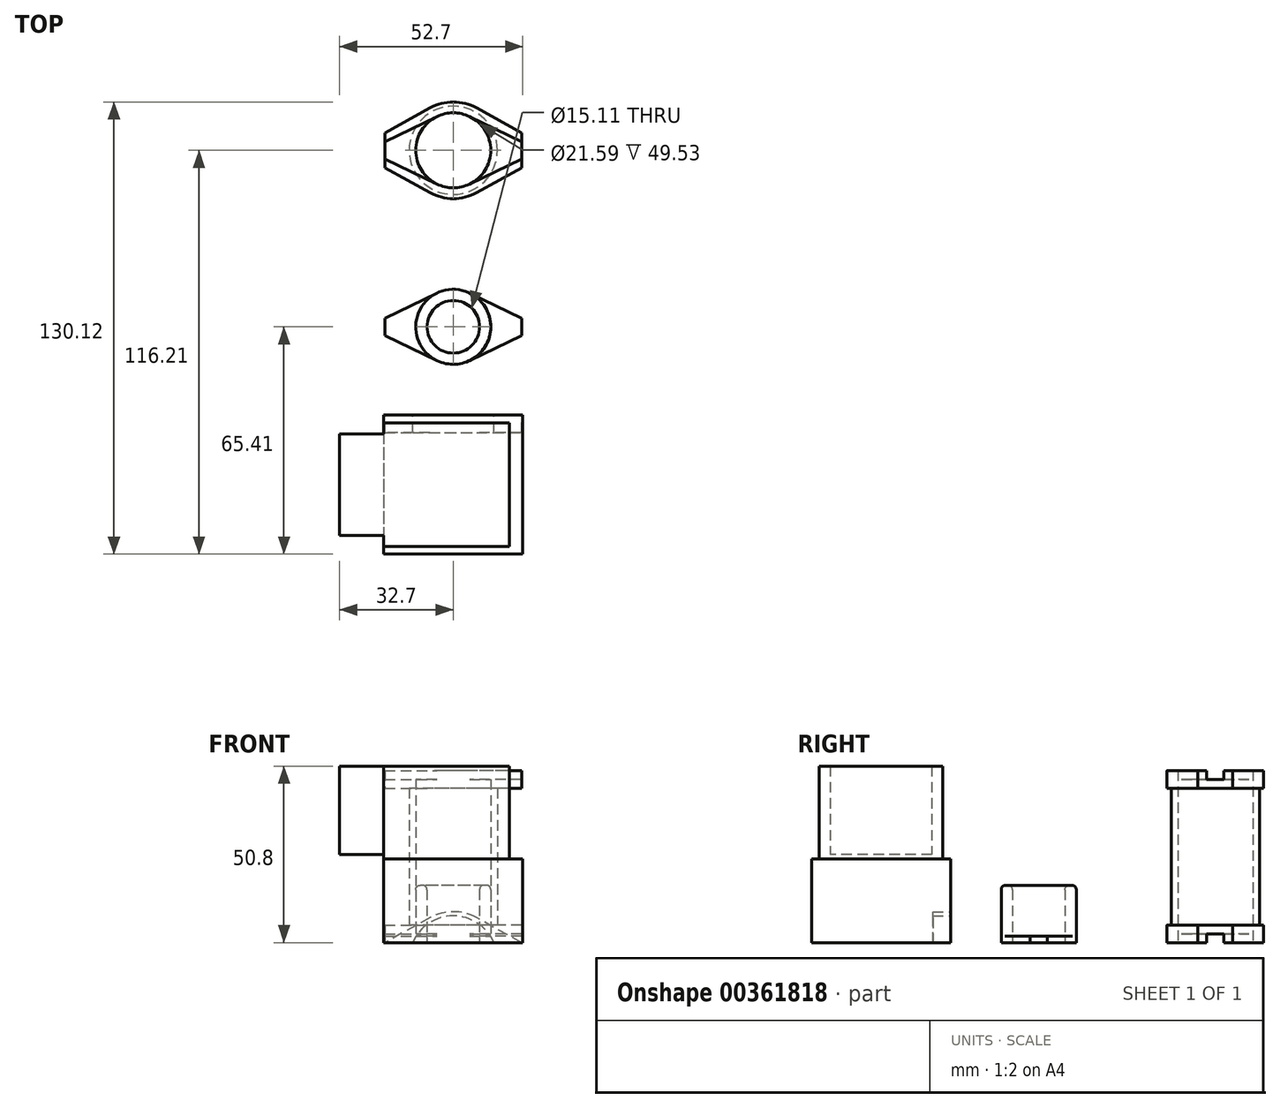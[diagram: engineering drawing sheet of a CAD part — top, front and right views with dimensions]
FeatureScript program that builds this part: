
annotation { "Feature Type Name" : "Feature", "Feature Type Description" : "" }
export const myFeature = defineFeature(function(context is Context, id is Id, definition is map)
    precondition{}
    {
        {
            var Q0;
            Q0=qCreatedBy(makeId("Top.planeOp"),FACE);
            var sketch = newSketch(context, id + "F0", { "sketchPlane" : qUnion([Q0])});
            skCircle(sketch, "E0", {"center": v(0, 0) * mm, "radius": 7.56 * mm});
            skCircle(sketch, "E1", {"center": v(0, 0) * mm, "radius": 10.8 * mm});
            skLineSegment(sketch, "E2", {"start": v(-19.69, 2.48) * mm, "end": v(-19.69, -2.48) * mm});
            skPoint(sketch, "E3", {"position": v(-19.69, 0) * mm});
            skLineSegment(sketch, "E4", {"start": v(-19.69, 2.48) * mm, "end": v(0, 11.99) * mm});
            skLineSegment(sketch, "E5", {"start": v(-19.69, -2.48) * mm, "end": v(0, -11.99) * mm});
            skPoint(sketch, "E6.MirrorP", {"position": v(19.69, 0) * mm});
            skLineSegment(sketch, "E7.MirrorCS", {"start": v(19.69, 2.48) * mm, "end": v(19.69, -2.48) * mm});
            skLineSegment(sketch, "E8.MirrorCS", {"start": v(19.69, 2.48) * mm, "end": v(0, 11.99) * mm});
            skLineSegment(sketch, "E9.MirrorCS", {"start": v(19.69, -2.48) * mm, "end": v(0, -11.99) * mm});
            skSolve(sketch);
        }
        {
            var Q0;
            {var subQ5=sQuery(id+"F0.wireOp",EDGE,"E2");Q0=makeQuery(id+"F0.imprint","IMPRINT",FACE,{"disambiguationData":[TD([[makeQuery(id+"F0.imprint","IMPRINT",EDGE,{"derivedFrom":subQ5}),1.0]])]});}
            var Q1;
            {var subQ5=sQuery(id+"F0.wireOp",EDGE,"E7.MirrorCS");Q1=makeQuery(id+"F0.imprint","IMPRINT",FACE,{"disambiguationData":[TD([[makeQuery(id+"F0.imprint","IMPRINT",EDGE,{"derivedFrom":subQ5}),-1.0]])]});}
            extrude(context, id + "F1", {"entities" : qUnion([Q0, Q1]), "depth" : 1.9 * mm, "offsetDistance" : 25.4 * mm});
        }
        {
            var Q0;
            Q0=makeQuery(id+"F0.imprint","IMPRINT",FACE,{"disambiguationData":[TD([[makeQuery(id+"F0.imprint","IMPRINT",EDGE,{"derivedFrom":sQuery(id+"F0.wireOp",EDGE,"E0")}),-1.0]])]});
            extrude(context, id + "F2", {"entities" : qUnion([Q0]), "operationType" : NewBodyOperationType.ADD, "depth" : 16.5 * mm, "offsetDistance" : 25.4 * mm});
        }
        {
            var Q0;
            Q0=makeQuery(id+"F2.opExtrude","CAP_EDGE",EDGE,{"disambiguationData":[OSD([sQuery(id+"F0.wireOp",EDGE,"E0")])],"isStart":false});
            var Q1;
            Q1=makeQuery(id+"F2.opExtrude","CAP_EDGE",EDGE,{"disambiguationData":[OSD([sQuery(id+"F0.wireOp",EDGE,"E1")])],"isStart":false});
            fillet(context, id + "F3", {"entities" : qUnion([Q0, Q1]), "radius" : 1.27 * mm, "tangentPropagation" : true, "allowEdgeOverflow" : false});
        }
        {
            var Q0;
            Q0=qCreatedBy(makeId("Top.planeOp"),FACE);
            var sketch = newSketch(context, id + "F4", { "sketchPlane" : qUnion([Q0])});
            skCircle(sketch, "E10", {"center": v(0, 50.8) * mm, "radius": 10.8 * mm});
            skLineSegment(sketch, "E11", {"start": v(-19.69, 53.28) * mm, "end": v(-19.69, 48.32) * mm});
            skPoint(sketch, "E12", {"position": v(-19.69, 50.8) * mm});
            skLineSegment(sketch, "E13", {"start": v(-19.69, 50.8) * mm, "end": v(0, 50.8) * mm, "construction": true});
            skLineSegment(sketch, "E14", {"start": v(0, 0) * mm, "end": v(-19.69, 0) * mm, "construction": true});
            skLineSegment(sketch, "E15", {"start": v(-19.69, 53.28) * mm, "end": v(0, 62.79) * mm});
            skLineSegment(sketch, "E16", {"start": v(-19.69, 48.32) * mm, "end": v(0, 38.81) * mm});
            skLineSegment(sketch, "E17.MirrorCS", {"start": v(19.69, 53.28) * mm, "end": v(19.69, 48.32) * mm});
            skPoint(sketch, "E18.MirrorP", {"position": v(19.69, 50.8) * mm});
            skLineSegment(sketch, "E19.MirrorCS", {"start": v(19.69, 53.28) * mm, "end": v(0, 62.79) * mm});
            skLineSegment(sketch, "E20.MirrorCS", {"start": v(19.69, 48.32) * mm, "end": v(0, 38.81) * mm});
            skLineSegment(sketch, "E21.MirrorCS", {"start": v(19.69, 50.8) * mm, "end": v(0, 50.8) * mm, "construction": true});
            skCircle(sketch, "E22", {"center": v(0, 50.8) * mm, "radius": 13.9 * mm});
            skLineSegment(sketch, "E23", {"start": v(-19.68, 55.82) * mm, "end": v(-19.68, 45.78) * mm});
            skPoint(sketch, "E24", {"position": v(-19.68, 50.8) * mm});
            skLineSegment(sketch, "E25", {"start": v(-19.68, 50.8) * mm, "end": v(0, 50.8) * mm, "construction": true});
            skLineSegment(sketch, "E26", {"start": v(-19.68, 55.82) * mm, "end": v(0, 66.69) * mm});
            skLineSegment(sketch, "E27", {"start": v(-19.69, 45.78) * mm, "end": v(0, 34.91) * mm});
            skLineSegment(sketch, "E28.MirrorCS", {"start": v(19.68, 55.82) * mm, "end": v(19.68, 45.78) * mm});
            skPoint(sketch, "E29.MirrorP", {"position": v(19.68, 50.8) * mm});
            skLineSegment(sketch, "E30.MirrorCS", {"start": v(19.68, 55.82) * mm, "end": v(0, 66.69) * mm});
            skLineSegment(sketch, "E31.MirrorCS", {"start": v(19.68, 45.78) * mm, "end": v(0, 34.91) * mm});
            skLineSegment(sketch, "E32.MirrorCS", {"start": v(19.68, 50.8) * mm, "end": v(0, 50.8) * mm, "construction": true});
            skCircle(sketch, "E33", {"center": v(0, 50.8) * mm, "radius": 12.7 * mm});
            skSolve(sketch);
        }
        {
            var Q0;
            {var subQ0=sQuery(id+"F4.wireOp",EDGE,"E23");var subQ1=sQuery(id+"F4.wireOp",EDGE,"E16");var subQ2=makeQuery(id+"F4.imprint","INTERSECT",VERTEX,{"derivedFrom":[subQ1,subQ0]});Q0=makeQuery(id+"F4.imprint","IMPRINT",FACE,{"disambiguationData":[TD([[makeQuery(id+"F4.imprint","IMPRINT",EDGE,{"disambiguationData":[TD([[subQ2,-1.0]])],"derivedFrom":subQ1}),-1.0]])]});}
            var Q1;
            {var subQ0=sQuery(id+"F4.wireOp",EDGE,"E28.MirrorCS");var subQ1=sQuery(id+"F4.wireOp",EDGE,"E20.MirrorCS");var subQ2=makeQuery(id+"F4.imprint","INTERSECT",VERTEX,{"derivedFrom":[subQ1,subQ0]});Q1=makeQuery(id+"F4.imprint","IMPRINT",FACE,{"disambiguationData":[TD([[makeQuery(id+"F4.imprint","IMPRINT",EDGE,{"disambiguationData":[TD([[subQ2,-1.0]])],"derivedFrom":subQ1}),1.0]])]});}
            var Q2;
            {var subQ0=sQuery(id+"F4.wireOp",EDGE,"E28.MirrorCS");var subQ1=sQuery(id+"F4.wireOp",EDGE,"E19.MirrorCS");var subQ2=makeQuery(id+"F4.imprint","INTERSECT",VERTEX,{"derivedFrom":[subQ1,subQ0]});Q2=makeQuery(id+"F4.imprint","IMPRINT",FACE,{"disambiguationData":[TD([[makeQuery(id+"F4.imprint","IMPRINT",EDGE,{"disambiguationData":[TD([[subQ2,-1.0]])],"derivedFrom":subQ1}),-1.0]])]});}
            var Q3;
            {var subQ0=sQuery(id+"F4.wireOp",EDGE,"E23");var subQ1=sQuery(id+"F4.wireOp",EDGE,"E15");var subQ2=makeQuery(id+"F4.imprint","INTERSECT",VERTEX,{"derivedFrom":[subQ1,subQ0]});Q3=makeQuery(id+"F4.imprint","IMPRINT",FACE,{"disambiguationData":[TD([[makeQuery(id+"F4.imprint","IMPRINT",EDGE,{"disambiguationData":[TD([[subQ2,-1.0]])],"derivedFrom":subQ1}),1.0]])]});}
            var Q4;
            {var subQ0=sQuery(id+"F4.wireOp",EDGE,"E23");var subQ1=sQuery(id+"F4.wireOp",EDGE,"E15");var subQ2=makeQuery(id+"F4.imprint","INTERSECT",VERTEX,{"derivedFrom":[subQ1,subQ0]});Q4=makeQuery(id+"F4.imprint","IMPRINT",FACE,{"disambiguationData":[TD([[makeQuery(id+"F4.imprint","IMPRINT",EDGE,{"disambiguationData":[TD([[subQ2,-1.0]])],"derivedFrom":subQ1}),-1.0]])]});}
            var Q5;
            {var subQ0=sQuery(id+"F4.wireOp",EDGE,"E28.MirrorCS");var subQ1=sQuery(id+"F4.wireOp",EDGE,"E19.MirrorCS");var subQ2=makeQuery(id+"F4.imprint","INTERSECT",VERTEX,{"derivedFrom":[subQ1,subQ0]});Q5=makeQuery(id+"F4.imprint","IMPRINT",FACE,{"disambiguationData":[TD([[makeQuery(id+"F4.imprint","IMPRINT",EDGE,{"disambiguationData":[TD([[subQ2,-1.0]])],"derivedFrom":subQ1}),1.0]])]});}
            var Q6;
            {var subQ0=sQuery(id+"F4.wireOp",EDGE,"E22");var subQ1=sQuery(id+"F4.wireOp",EDGE,"E15");var subQ2=makeQuery(id+"F4.imprint","INTERSECT",VERTEX,{"derivedFrom":[subQ1,subQ0]});Q6=makeQuery(id+"F4.imprint","IMPRINT",FACE,{"disambiguationData":[TD([[makeQuery(id+"F4.imprint","IMPRINT",EDGE,{"disambiguationData":[TD([[subQ2,-1.0]])],"derivedFrom":subQ1}),-1.0]])]});}
            var Q7;
            {var subQ0=sQuery(id+"F4.wireOp",EDGE,"E22");var subQ7=sQuery(id+"F4.wireOp",EDGE,"E15");var subQ9=makeQuery(id+"F4.imprint","INTERSECT",VERTEX,{"derivedFrom":[subQ7,subQ0]});Q7=makeQuery(id+"F4.imprint","IMPRINT",FACE,{"disambiguationData":[TD([[makeQuery(id+"F4.imprint","IMPRINT",EDGE,{"disambiguationData":[TD([[subQ9,-1.0]])],"derivedFrom":subQ7}),1.0]])]});}
            var Q8;
            {var subQ0=sQuery(id+"F4.wireOp",EDGE,"E15");var subQ1=sQuery(id+"F4.wireOp",EDGE,"E10");var subQ2=makeQuery(id+"F4.imprint","INTERSECT",VERTEX,{"derivedFrom":[subQ1,subQ0]});Q8=makeQuery(id+"F4.imprint","IMPRINT",FACE,{"disambiguationData":[TD([[makeQuery(id+"F4.imprint","IMPRINT",EDGE,{"disambiguationData":[TD([[subQ2,-1.0]])],"derivedFrom":subQ1}),-1.0]])]});}
            var Q9;
            {var subQ1=sQuery(id+"F4.wireOp",EDGE,"E15");var subQ3=sQuery(id+"F4.wireOp",EDGE,"E10");var subQ7=makeQuery(id+"F4.imprint","INTERSECT",VERTEX,{"derivedFrom":[subQ3,subQ1]});Q9=makeQuery(id+"F4.imprint","IMPRINT",FACE,{"disambiguationData":[TD([[makeQuery(id+"F4.imprint","IMPRINT",EDGE,{"disambiguationData":[TD([[subQ7,1.0]])],"derivedFrom":subQ1}),1.0]])]});}
            var Q10;
            {var subQ0=sQuery(id+"F4.wireOp",EDGE,"E15");var subQ1=sQuery(id+"F4.wireOp",EDGE,"E10");var subQ2=makeQuery(id+"F4.imprint","INTERSECT",VERTEX,{"derivedFrom":[subQ1,subQ0]});Q10=makeQuery(id+"F4.imprint","IMPRINT",FACE,{"disambiguationData":[TD([[makeQuery(id+"F4.imprint","IMPRINT",EDGE,{"disambiguationData":[TD([[subQ2,1.0]])],"derivedFrom":subQ1}),-1.0]])]});}
            var Q11;
            {var subQ0=sQuery(id+"F4.wireOp",EDGE,"E10");var subQ1=makeQuery(id+"F4.imprint","INTERSECT",VERTEX,{"derivedFrom":[subQ0,sQuery(id+"F4.wireOp",EDGE,"E15")]});Q11=makeQuery(id+"F4.imprint","IMPRINT",FACE,{"disambiguationData":[TD([[makeQuery(id+"F4.imprint","IMPRINT",EDGE,{"disambiguationData":[TD([[subQ1,1.0]])],"derivedFrom":subQ0}),1.0]])]});}
            var Q12;
            {var subQ0=sQuery(id+"F4.wireOp",EDGE,"E16");var subQ1=sQuery(id+"F4.wireOp",EDGE,"E10");var subQ2=makeQuery(id+"F4.imprint","INTERSECT",VERTEX,{"derivedFrom":[subQ1,subQ0]});Q12=makeQuery(id+"F4.imprint","IMPRINT",FACE,{"disambiguationData":[TD([[makeQuery(id+"F4.imprint","IMPRINT",EDGE,{"disambiguationData":[TD([[subQ2,-1.0]])],"derivedFrom":subQ1}),-1.0]])]});}
            var Q13;
            {var subQ1=sQuery(id+"F4.wireOp",EDGE,"E16");var subQ3=sQuery(id+"F4.wireOp",EDGE,"E10");var subQ7=makeQuery(id+"F4.imprint","INTERSECT",VERTEX,{"derivedFrom":[subQ3,subQ1]});Q13=makeQuery(id+"F4.imprint","IMPRINT",FACE,{"disambiguationData":[TD([[makeQuery(id+"F4.imprint","IMPRINT",EDGE,{"disambiguationData":[TD([[subQ7,1.0]])],"derivedFrom":subQ1}),-1.0]])]});}
            var Q14;
            {var subQ0=sQuery(id+"F4.wireOp",EDGE,"E22");var subQ7=sQuery(id+"F4.wireOp",EDGE,"E16");var subQ8=makeQuery(id+"F4.imprint","INTERSECT",VERTEX,{"derivedFrom":[subQ7,subQ0]});Q14=makeQuery(id+"F4.imprint","IMPRINT",FACE,{"disambiguationData":[TD([[makeQuery(id+"F4.imprint","IMPRINT",EDGE,{"disambiguationData":[TD([[subQ8,-1.0]])],"derivedFrom":subQ7}),-1.0]])]});}
            var Q15;
            {var subQ0=sQuery(id+"F4.wireOp",EDGE,"E19.MirrorCS");var subQ1=sQuery(id+"F4.wireOp",EDGE,"E10");var subQ2=makeQuery(id+"F4.imprint","INTERSECT",VERTEX,{"derivedFrom":[subQ1,subQ0]});Q15=makeQuery(id+"F4.imprint","IMPRINT",FACE,{"disambiguationData":[TD([[makeQuery(id+"F4.imprint","IMPRINT",EDGE,{"disambiguationData":[TD([[subQ2,1.0]])],"derivedFrom":subQ1}),-1.0]])]});}
            var Q16;
            {var subQ0=sQuery(id+"F4.wireOp",EDGE,"E22");var subQ1=sQuery(id+"F4.wireOp",EDGE,"E19.MirrorCS");var subQ2=makeQuery(id+"F4.imprint","INTERSECT",VERTEX,{"derivedFrom":[subQ1,subQ0]});Q16=makeQuery(id+"F4.imprint","IMPRINT",FACE,{"disambiguationData":[TD([[makeQuery(id+"F4.imprint","IMPRINT",EDGE,{"disambiguationData":[TD([[subQ2,-1.0]])],"derivedFrom":subQ1}),1.0]])]});}
            extrude(context, id + "F5", {"entities" : qUnion([Q0, Q1, Q2, Q3, Q4, Q5, Q6, Q7, Q8, Q9, Q10, Q11, Q12, Q13, Q14, Q15, Q16]), "depth" : 49.53 * mm, "offsetDistance" : 25.4 * mm});
        }
        {
            var Q0;
            {var subQ0=sQuery(id+"F4.wireOp",EDGE,"E23");var subQ1=sQuery(id+"F4.wireOp",EDGE,"E16");var subQ2=makeQuery(id+"F4.imprint","INTERSECT",VERTEX,{"derivedFrom":[subQ1,subQ0]});Q0=makeQuery(id+"F4.imprint","IMPRINT",FACE,{"disambiguationData":[TD([[makeQuery(id+"F4.imprint","IMPRINT",EDGE,{"disambiguationData":[TD([[subQ2,-1.0]])],"derivedFrom":subQ1}),-1.0]])]});}
            var Q1;
            {var subQ0=sQuery(id+"F4.wireOp",EDGE,"E23");var subQ1=sQuery(id+"F4.wireOp",EDGE,"E15");var subQ2=makeQuery(id+"F4.imprint","INTERSECT",VERTEX,{"derivedFrom":[subQ1,subQ0]});Q1=makeQuery(id+"F4.imprint","IMPRINT",FACE,{"disambiguationData":[TD([[makeQuery(id+"F4.imprint","IMPRINT",EDGE,{"disambiguationData":[TD([[subQ2,-1.0]])],"derivedFrom":subQ1}),-1.0]])]});}
            var Q2;
            {var subQ0=sQuery(id+"F4.wireOp",EDGE,"E23");var subQ1=sQuery(id+"F4.wireOp",EDGE,"E15");var subQ2=makeQuery(id+"F4.imprint","INTERSECT",VERTEX,{"derivedFrom":[subQ1,subQ0]});Q2=makeQuery(id+"F4.imprint","IMPRINT",FACE,{"disambiguationData":[TD([[makeQuery(id+"F4.imprint","IMPRINT",EDGE,{"disambiguationData":[TD([[subQ2,-1.0]])],"derivedFrom":subQ1}),1.0]])]});}
            var Q3;
            {var subQ0=sQuery(id+"F4.wireOp",EDGE,"E28.MirrorCS");var subQ1=sQuery(id+"F4.wireOp",EDGE,"E19.MirrorCS");var subQ2=makeQuery(id+"F4.imprint","INTERSECT",VERTEX,{"derivedFrom":[subQ1,subQ0]});Q3=makeQuery(id+"F4.imprint","IMPRINT",FACE,{"disambiguationData":[TD([[makeQuery(id+"F4.imprint","IMPRINT",EDGE,{"disambiguationData":[TD([[subQ2,-1.0]])],"derivedFrom":subQ1}),-1.0]])]});}
            var Q4;
            {var subQ0=sQuery(id+"F4.wireOp",EDGE,"E28.MirrorCS");var subQ1=sQuery(id+"F4.wireOp",EDGE,"E19.MirrorCS");var subQ2=makeQuery(id+"F4.imprint","INTERSECT",VERTEX,{"derivedFrom":[subQ1,subQ0]});Q4=makeQuery(id+"F4.imprint","IMPRINT",FACE,{"disambiguationData":[TD([[makeQuery(id+"F4.imprint","IMPRINT",EDGE,{"disambiguationData":[TD([[subQ2,-1.0]])],"derivedFrom":subQ1}),1.0]])]});}
            var Q5;
            {var subQ0=sQuery(id+"F4.wireOp",EDGE,"E28.MirrorCS");var subQ1=sQuery(id+"F4.wireOp",EDGE,"E20.MirrorCS");var subQ2=makeQuery(id+"F4.imprint","INTERSECT",VERTEX,{"derivedFrom":[subQ1,subQ0]});Q5=makeQuery(id+"F4.imprint","IMPRINT",FACE,{"disambiguationData":[TD([[makeQuery(id+"F4.imprint","IMPRINT",EDGE,{"disambiguationData":[TD([[subQ2,-1.0]])],"derivedFrom":subQ1}),1.0]])]});}
            var Q6;
            {var subQ0=sQuery(id+"F4.wireOp",EDGE,"E22");var subQ7=sQuery(id+"F4.wireOp",EDGE,"E16");var subQ8=makeQuery(id+"F4.imprint","INTERSECT",VERTEX,{"derivedFrom":[subQ7,subQ0]});Q6=makeQuery(id+"F4.imprint","IMPRINT",FACE,{"disambiguationData":[TD([[makeQuery(id+"F4.imprint","IMPRINT",EDGE,{"disambiguationData":[TD([[subQ8,-1.0]])],"derivedFrom":subQ7}),-1.0]])]});}
            var Q7;
            {var subQ0=sQuery(id+"F4.wireOp",EDGE,"E22");var subQ7=sQuery(id+"F4.wireOp",EDGE,"E15");var subQ9=makeQuery(id+"F4.imprint","INTERSECT",VERTEX,{"derivedFrom":[subQ7,subQ0]});Q7=makeQuery(id+"F4.imprint","IMPRINT",FACE,{"disambiguationData":[TD([[makeQuery(id+"F4.imprint","IMPRINT",EDGE,{"disambiguationData":[TD([[subQ9,-1.0]])],"derivedFrom":subQ7}),1.0]])]});}
            var Q8;
            {var subQ0=sQuery(id+"F4.wireOp",EDGE,"E22");var subQ1=sQuery(id+"F4.wireOp",EDGE,"E19.MirrorCS");var subQ2=makeQuery(id+"F4.imprint","INTERSECT",VERTEX,{"derivedFrom":[subQ1,subQ0]});Q8=makeQuery(id+"F4.imprint","IMPRINT",FACE,{"disambiguationData":[TD([[makeQuery(id+"F4.imprint","IMPRINT",EDGE,{"disambiguationData":[TD([[subQ2,-1.0]])],"derivedFrom":subQ1}),1.0]])]});}
            var Q9;
            {var subQ0=sQuery(id+"F4.wireOp",EDGE,"E22");var subQ1=sQuery(id+"F4.wireOp",EDGE,"E15");var subQ2=makeQuery(id+"F4.imprint","INTERSECT",VERTEX,{"derivedFrom":[subQ1,subQ0]});Q9=makeQuery(id+"F4.imprint","IMPRINT",FACE,{"disambiguationData":[TD([[makeQuery(id+"F4.imprint","IMPRINT",EDGE,{"disambiguationData":[TD([[subQ2,-1.0]])],"derivedFrom":subQ1}),-1.0]])]});}
            extrude(context, id + "F6", {"entities" : qUnion([Q0, Q1, Q2, Q3, Q4, Q5, Q6, Q7, Q8, Q9]), "operationType" : NewBodyOperationType.REMOVE, "depth" : 44.45 * mm, "offsetDistance" : 25.4 * mm});
        }
        {
            var Q0;
            {var subQ0=sQuery(id+"F4.wireOp",EDGE,"E23");var subQ1=sQuery(id+"F4.wireOp",EDGE,"E16");var subQ2=makeQuery(id+"F4.imprint","INTERSECT",VERTEX,{"derivedFrom":[subQ1,subQ0]});Q0=makeQuery(id+"F4.imprint","IMPRINT",FACE,{"disambiguationData":[TD([[makeQuery(id+"F4.imprint","IMPRINT",EDGE,{"disambiguationData":[TD([[subQ2,-1.0]])],"derivedFrom":subQ1}),-1.0]])]});}
            var Q1;
            {var subQ0=sQuery(id+"F4.wireOp",EDGE,"E22");var subQ7=sQuery(id+"F4.wireOp",EDGE,"E16");var subQ8=makeQuery(id+"F4.imprint","INTERSECT",VERTEX,{"derivedFrom":[subQ7,subQ0]});Q1=makeQuery(id+"F4.imprint","IMPRINT",FACE,{"disambiguationData":[TD([[makeQuery(id+"F4.imprint","IMPRINT",EDGE,{"disambiguationData":[TD([[subQ8,-1.0]])],"derivedFrom":subQ7}),-1.0]])]});}
            var Q2;
            {var subQ1=sQuery(id+"F4.wireOp",EDGE,"E16");var subQ3=sQuery(id+"F4.wireOp",EDGE,"E10");var subQ7=makeQuery(id+"F4.imprint","INTERSECT",VERTEX,{"derivedFrom":[subQ3,subQ1]});Q2=makeQuery(id+"F4.imprint","IMPRINT",FACE,{"disambiguationData":[TD([[makeQuery(id+"F4.imprint","IMPRINT",EDGE,{"disambiguationData":[TD([[subQ7,1.0]])],"derivedFrom":subQ1}),-1.0]])]});}
            var Q3;
            {var subQ0=sQuery(id+"F4.wireOp",EDGE,"E15");var subQ1=sQuery(id+"F4.wireOp",EDGE,"E10");var subQ2=makeQuery(id+"F4.imprint","INTERSECT",VERTEX,{"derivedFrom":[subQ1,subQ0]});Q3=makeQuery(id+"F4.imprint","IMPRINT",FACE,{"disambiguationData":[TD([[makeQuery(id+"F4.imprint","IMPRINT",EDGE,{"disambiguationData":[TD([[subQ2,-1.0]])],"derivedFrom":subQ1}),-1.0]])]});}
            var Q4;
            {var subQ0=sQuery(id+"F4.wireOp",EDGE,"E22");var subQ1=sQuery(id+"F4.wireOp",EDGE,"E15");var subQ2=makeQuery(id+"F4.imprint","INTERSECT",VERTEX,{"derivedFrom":[subQ1,subQ0]});Q4=makeQuery(id+"F4.imprint","IMPRINT",FACE,{"disambiguationData":[TD([[makeQuery(id+"F4.imprint","IMPRINT",EDGE,{"disambiguationData":[TD([[subQ2,-1.0]])],"derivedFrom":subQ1}),-1.0]])]});}
            var Q5;
            {var subQ0=sQuery(id+"F4.wireOp",EDGE,"E23");var subQ1=sQuery(id+"F4.wireOp",EDGE,"E15");var subQ2=makeQuery(id+"F4.imprint","INTERSECT",VERTEX,{"derivedFrom":[subQ1,subQ0]});Q5=makeQuery(id+"F4.imprint","IMPRINT",FACE,{"disambiguationData":[TD([[makeQuery(id+"F4.imprint","IMPRINT",EDGE,{"disambiguationData":[TD([[subQ2,-1.0]])],"derivedFrom":subQ1}),-1.0]])]});}
            var Q6;
            {var subQ0=sQuery(id+"F4.wireOp",EDGE,"E23");var subQ1=sQuery(id+"F4.wireOp",EDGE,"E15");var subQ2=makeQuery(id+"F4.imprint","INTERSECT",VERTEX,{"derivedFrom":[subQ1,subQ0]});Q6=makeQuery(id+"F4.imprint","IMPRINT",FACE,{"disambiguationData":[TD([[makeQuery(id+"F4.imprint","IMPRINT",EDGE,{"disambiguationData":[TD([[subQ2,-1.0]])],"derivedFrom":subQ1}),1.0]])]});}
            var Q7;
            {var subQ1=sQuery(id+"F4.wireOp",EDGE,"E15");var subQ3=sQuery(id+"F4.wireOp",EDGE,"E10");var subQ7=makeQuery(id+"F4.imprint","INTERSECT",VERTEX,{"derivedFrom":[subQ3,subQ1]});Q7=makeQuery(id+"F4.imprint","IMPRINT",FACE,{"disambiguationData":[TD([[makeQuery(id+"F4.imprint","IMPRINT",EDGE,{"disambiguationData":[TD([[subQ7,1.0]])],"derivedFrom":subQ1}),1.0]])]});}
            var Q8;
            {var subQ0=sQuery(id+"F4.wireOp",EDGE,"E22");var subQ7=sQuery(id+"F4.wireOp",EDGE,"E15");var subQ9=makeQuery(id+"F4.imprint","INTERSECT",VERTEX,{"derivedFrom":[subQ7,subQ0]});Q8=makeQuery(id+"F4.imprint","IMPRINT",FACE,{"disambiguationData":[TD([[makeQuery(id+"F4.imprint","IMPRINT",EDGE,{"disambiguationData":[TD([[subQ9,-1.0]])],"derivedFrom":subQ7}),1.0]])]});}
            var Q9;
            {var subQ0=sQuery(id+"F4.wireOp",EDGE,"E15");var subQ1=sQuery(id+"F4.wireOp",EDGE,"E10");var subQ2=makeQuery(id+"F4.imprint","INTERSECT",VERTEX,{"derivedFrom":[subQ1,subQ0]});Q9=makeQuery(id+"F4.imprint","IMPRINT",FACE,{"disambiguationData":[TD([[makeQuery(id+"F4.imprint","IMPRINT",EDGE,{"disambiguationData":[TD([[subQ2,1.0]])],"derivedFrom":subQ1}),-1.0]])]});}
            var Q10;
            {var subQ0=sQuery(id+"F4.wireOp",EDGE,"E10");var subQ1=makeQuery(id+"F4.imprint","INTERSECT",VERTEX,{"derivedFrom":[subQ0,sQuery(id+"F4.wireOp",EDGE,"E15")]});Q10=makeQuery(id+"F4.imprint","IMPRINT",FACE,{"disambiguationData":[TD([[makeQuery(id+"F4.imprint","IMPRINT",EDGE,{"disambiguationData":[TD([[subQ1,1.0]])],"derivedFrom":subQ0}),1.0]])]});}
            var Q11;
            {var subQ0=sQuery(id+"F4.wireOp",EDGE,"E19.MirrorCS");var subQ1=sQuery(id+"F4.wireOp",EDGE,"E10");var subQ2=makeQuery(id+"F4.imprint","INTERSECT",VERTEX,{"derivedFrom":[subQ1,subQ0]});Q11=makeQuery(id+"F4.imprint","IMPRINT",FACE,{"disambiguationData":[TD([[makeQuery(id+"F4.imprint","IMPRINT",EDGE,{"disambiguationData":[TD([[subQ2,1.0]])],"derivedFrom":subQ1}),-1.0]])]});}
            var Q12;
            {var subQ0=sQuery(id+"F4.wireOp",EDGE,"E22");var subQ1=sQuery(id+"F4.wireOp",EDGE,"E19.MirrorCS");var subQ2=makeQuery(id+"F4.imprint","INTERSECT",VERTEX,{"derivedFrom":[subQ1,subQ0]});Q12=makeQuery(id+"F4.imprint","IMPRINT",FACE,{"disambiguationData":[TD([[makeQuery(id+"F4.imprint","IMPRINT",EDGE,{"disambiguationData":[TD([[subQ2,-1.0]])],"derivedFrom":subQ1}),1.0]])]});}
            var Q13;
            {var subQ0=sQuery(id+"F4.wireOp",EDGE,"E28.MirrorCS");var subQ1=sQuery(id+"F4.wireOp",EDGE,"E19.MirrorCS");var subQ2=makeQuery(id+"F4.imprint","INTERSECT",VERTEX,{"derivedFrom":[subQ1,subQ0]});Q13=makeQuery(id+"F4.imprint","IMPRINT",FACE,{"disambiguationData":[TD([[makeQuery(id+"F4.imprint","IMPRINT",EDGE,{"disambiguationData":[TD([[subQ2,-1.0]])],"derivedFrom":subQ1}),1.0]])]});}
            var Q14;
            {var subQ0=sQuery(id+"F4.wireOp",EDGE,"E28.MirrorCS");var subQ1=sQuery(id+"F4.wireOp",EDGE,"E19.MirrorCS");var subQ2=makeQuery(id+"F4.imprint","INTERSECT",VERTEX,{"derivedFrom":[subQ1,subQ0]});Q14=makeQuery(id+"F4.imprint","IMPRINT",FACE,{"disambiguationData":[TD([[makeQuery(id+"F4.imprint","IMPRINT",EDGE,{"disambiguationData":[TD([[subQ2,-1.0]])],"derivedFrom":subQ1}),-1.0]])]});}
            var Q15;
            {var subQ0=sQuery(id+"F4.wireOp",EDGE,"E28.MirrorCS");var subQ1=sQuery(id+"F4.wireOp",EDGE,"E20.MirrorCS");var subQ2=makeQuery(id+"F4.imprint","INTERSECT",VERTEX,{"derivedFrom":[subQ1,subQ0]});Q15=makeQuery(id+"F4.imprint","IMPRINT",FACE,{"disambiguationData":[TD([[makeQuery(id+"F4.imprint","IMPRINT",EDGE,{"disambiguationData":[TD([[subQ2,-1.0]])],"derivedFrom":subQ1}),1.0]])]});}
            var Q16;
            {var subQ0=sQuery(id+"F4.wireOp",EDGE,"E16");var subQ1=sQuery(id+"F4.wireOp",EDGE,"E10");var subQ2=makeQuery(id+"F4.imprint","INTERSECT",VERTEX,{"derivedFrom":[subQ1,subQ0]});Q16=makeQuery(id+"F4.imprint","IMPRINT",FACE,{"disambiguationData":[TD([[makeQuery(id+"F4.imprint","IMPRINT",EDGE,{"disambiguationData":[TD([[subQ2,-1.0]])],"derivedFrom":subQ1}),-1.0]])]});}
            extrude(context, id + "F7", {"entities" : qUnion([Q0, Q1, Q2, Q3, Q4, Q5, Q6, Q7, Q8, Q9, Q10, Q11, Q12, Q13, Q14, Q15, Q16]), "operationType" : NewBodyOperationType.ADD, "depth" : 5.08 * mm, "offsetDistance" : 25.4 * mm});
        }
        {
            var Q0;
            {var subQ0=sQuery(id+"F4.wireOp",EDGE,"E23");var subQ1=sQuery(id+"F4.wireOp",EDGE,"E15");var subQ2=makeQuery(id+"F4.imprint","INTERSECT",VERTEX,{"derivedFrom":[subQ1,subQ0]});Q0=makeQuery(id+"F4.imprint","IMPRINT",FACE,{"disambiguationData":[TD([[makeQuery(id+"F4.imprint","IMPRINT",EDGE,{"disambiguationData":[TD([[subQ2,-1.0]])],"derivedFrom":subQ1}),-1.0]])]});}
            var Q1;
            {var subQ0=sQuery(id+"F4.wireOp",EDGE,"E22");var subQ1=sQuery(id+"F4.wireOp",EDGE,"E15");var subQ2=makeQuery(id+"F4.imprint","INTERSECT",VERTEX,{"derivedFrom":[subQ1,subQ0]});Q1=makeQuery(id+"F4.imprint","IMPRINT",FACE,{"disambiguationData":[TD([[makeQuery(id+"F4.imprint","IMPRINT",EDGE,{"disambiguationData":[TD([[subQ2,-1.0]])],"derivedFrom":subQ1}),-1.0]])]});}
            var Q2;
            {var subQ0=sQuery(id+"F4.wireOp",EDGE,"E15");var subQ1=sQuery(id+"F4.wireOp",EDGE,"E10");var subQ2=makeQuery(id+"F4.imprint","INTERSECT",VERTEX,{"derivedFrom":[subQ1,subQ0]});Q2=makeQuery(id+"F4.imprint","IMPRINT",FACE,{"disambiguationData":[TD([[makeQuery(id+"F4.imprint","IMPRINT",EDGE,{"disambiguationData":[TD([[subQ2,-1.0]])],"derivedFrom":subQ1}),-1.0]])]});}
            var Q3;
            {var subQ0=sQuery(id+"F4.wireOp",EDGE,"E10");var subQ1=makeQuery(id+"F4.imprint","INTERSECT",VERTEX,{"derivedFrom":[subQ0,sQuery(id+"F4.wireOp",EDGE,"E15")]});Q3=makeQuery(id+"F4.imprint","IMPRINT",FACE,{"disambiguationData":[TD([[makeQuery(id+"F4.imprint","IMPRINT",EDGE,{"disambiguationData":[TD([[subQ1,1.0]])],"derivedFrom":subQ0}),1.0]])]});}
            var Q4;
            {var subQ0=sQuery(id+"F4.wireOp",EDGE,"E19.MirrorCS");var subQ1=sQuery(id+"F4.wireOp",EDGE,"E10");var subQ2=makeQuery(id+"F4.imprint","INTERSECT",VERTEX,{"derivedFrom":[subQ1,subQ0]});Q4=makeQuery(id+"F4.imprint","IMPRINT",FACE,{"disambiguationData":[TD([[makeQuery(id+"F4.imprint","IMPRINT",EDGE,{"disambiguationData":[TD([[subQ2,1.0]])],"derivedFrom":subQ1}),-1.0]])]});}
            var Q5;
            {var subQ0=sQuery(id+"F4.wireOp",EDGE,"E22");var subQ1=sQuery(id+"F4.wireOp",EDGE,"E19.MirrorCS");var subQ2=makeQuery(id+"F4.imprint","INTERSECT",VERTEX,{"derivedFrom":[subQ1,subQ0]});Q5=makeQuery(id+"F4.imprint","IMPRINT",FACE,{"disambiguationData":[TD([[makeQuery(id+"F4.imprint","IMPRINT",EDGE,{"disambiguationData":[TD([[subQ2,-1.0]])],"derivedFrom":subQ1}),1.0]])]});}
            var Q6;
            {var subQ0=sQuery(id+"F4.wireOp",EDGE,"E28.MirrorCS");var subQ1=sQuery(id+"F4.wireOp",EDGE,"E19.MirrorCS");var subQ2=makeQuery(id+"F4.imprint","INTERSECT",VERTEX,{"derivedFrom":[subQ1,subQ0]});Q6=makeQuery(id+"F4.imprint","IMPRINT",FACE,{"disambiguationData":[TD([[makeQuery(id+"F4.imprint","IMPRINT",EDGE,{"disambiguationData":[TD([[subQ2,-1.0]])],"derivedFrom":subQ1}),1.0]])]});}
            extrude(context, id + "F8", {"entities" : qUnion([Q0, Q1, Q2, Q3, Q4, Q5, Q6]), "operationType" : NewBodyOperationType.REMOVE, "depth" : 49.53 * mm, "offsetDistance" : 25.4 * mm});
        }
        {
            var Q0;
            {var subQ0=sQuery(id+"F4.wireOp",EDGE,"E23");var subQ1=sQuery(id+"F4.wireOp",EDGE,"E15");var subQ2=makeQuery(id+"F4.imprint","INTERSECT",VERTEX,{"derivedFrom":[subQ1,subQ0]});Q0=makeQuery(id+"F4.imprint","IMPRINT",FACE,{"disambiguationData":[TD([[makeQuery(id+"F4.imprint","IMPRINT",EDGE,{"disambiguationData":[TD([[subQ2,-1.0]])],"derivedFrom":subQ1}),-1.0]])]});}
            var Q1;
            {var subQ0=sQuery(id+"F4.wireOp",EDGE,"E22");var subQ1=sQuery(id+"F4.wireOp",EDGE,"E15");var subQ2=makeQuery(id+"F4.imprint","INTERSECT",VERTEX,{"derivedFrom":[subQ1,subQ0]});Q1=makeQuery(id+"F4.imprint","IMPRINT",FACE,{"disambiguationData":[TD([[makeQuery(id+"F4.imprint","IMPRINT",EDGE,{"disambiguationData":[TD([[subQ2,-1.0]])],"derivedFrom":subQ1}),-1.0]])]});}
            var Q2;
            {var subQ0=sQuery(id+"F4.wireOp",EDGE,"E15");var subQ1=sQuery(id+"F4.wireOp",EDGE,"E10");var subQ2=makeQuery(id+"F4.imprint","INTERSECT",VERTEX,{"derivedFrom":[subQ1,subQ0]});Q2=makeQuery(id+"F4.imprint","IMPRINT",FACE,{"disambiguationData":[TD([[makeQuery(id+"F4.imprint","IMPRINT",EDGE,{"disambiguationData":[TD([[subQ2,-1.0]])],"derivedFrom":subQ1}),-1.0]])]});}
            var Q3;
            {var subQ0=sQuery(id+"F4.wireOp",EDGE,"E10");var subQ1=makeQuery(id+"F4.imprint","INTERSECT",VERTEX,{"derivedFrom":[subQ0,sQuery(id+"F4.wireOp",EDGE,"E15")]});Q3=makeQuery(id+"F4.imprint","IMPRINT",FACE,{"disambiguationData":[TD([[makeQuery(id+"F4.imprint","IMPRINT",EDGE,{"disambiguationData":[TD([[subQ1,1.0]])],"derivedFrom":subQ0}),1.0]])]});}
            var Q4;
            {var subQ0=sQuery(id+"F4.wireOp",EDGE,"E19.MirrorCS");var subQ1=sQuery(id+"F4.wireOp",EDGE,"E10");var subQ2=makeQuery(id+"F4.imprint","INTERSECT",VERTEX,{"derivedFrom":[subQ1,subQ0]});Q4=makeQuery(id+"F4.imprint","IMPRINT",FACE,{"disambiguationData":[TD([[makeQuery(id+"F4.imprint","IMPRINT",EDGE,{"disambiguationData":[TD([[subQ2,1.0]])],"derivedFrom":subQ1}),-1.0]])]});}
            var Q5;
            {var subQ0=sQuery(id+"F4.wireOp",EDGE,"E22");var subQ1=sQuery(id+"F4.wireOp",EDGE,"E19.MirrorCS");var subQ2=makeQuery(id+"F4.imprint","INTERSECT",VERTEX,{"derivedFrom":[subQ1,subQ0]});Q5=makeQuery(id+"F4.imprint","IMPRINT",FACE,{"disambiguationData":[TD([[makeQuery(id+"F4.imprint","IMPRINT",EDGE,{"disambiguationData":[TD([[subQ2,-1.0]])],"derivedFrom":subQ1}),1.0]])]});}
            var Q6;
            {var subQ0=sQuery(id+"F4.wireOp",EDGE,"E28.MirrorCS");var subQ1=sQuery(id+"F4.wireOp",EDGE,"E19.MirrorCS");var subQ2=makeQuery(id+"F4.imprint","INTERSECT",VERTEX,{"derivedFrom":[subQ1,subQ0]});Q6=makeQuery(id+"F4.imprint","IMPRINT",FACE,{"disambiguationData":[TD([[makeQuery(id+"F4.imprint","IMPRINT",EDGE,{"disambiguationData":[TD([[subQ2,-1.0]])],"derivedFrom":subQ1}),1.0]])]});}
            extrude(context, id + "F9", {"entities" : qUnion([Q0, Q1, Q2, Q3, Q4, Q5, Q6]), "operationType" : NewBodyOperationType.ADD, "depth" : 47 * mm, "offsetDistance" : 25.4 * mm});
        }
        {
            var Q0;
            {var subQ0=sQuery(id+"F4.wireOp",EDGE,"E28.MirrorCS");var subQ1=sQuery(id+"F4.wireOp",EDGE,"E19.MirrorCS");var subQ2=makeQuery(id+"F4.imprint","INTERSECT",VERTEX,{"derivedFrom":[subQ1,subQ0]});Q0=makeQuery(id+"F4.imprint","IMPRINT",FACE,{"disambiguationData":[TD([[makeQuery(id+"F4.imprint","IMPRINT",EDGE,{"disambiguationData":[TD([[subQ2,-1.0]])],"derivedFrom":subQ1}),1.0]])]});}
            var Q1;
            {var subQ0=sQuery(id+"F4.wireOp",EDGE,"E22");var subQ1=sQuery(id+"F4.wireOp",EDGE,"E19.MirrorCS");var subQ2=makeQuery(id+"F4.imprint","INTERSECT",VERTEX,{"derivedFrom":[subQ1,subQ0]});Q1=makeQuery(id+"F4.imprint","IMPRINT",FACE,{"disambiguationData":[TD([[makeQuery(id+"F4.imprint","IMPRINT",EDGE,{"disambiguationData":[TD([[subQ2,-1.0]])],"derivedFrom":subQ1}),1.0]])]});}
            var Q2;
            {var subQ0=sQuery(id+"F4.wireOp",EDGE,"E23");var subQ1=sQuery(id+"F4.wireOp",EDGE,"E15");var subQ2=makeQuery(id+"F4.imprint","INTERSECT",VERTEX,{"derivedFrom":[subQ1,subQ0]});Q2=makeQuery(id+"F4.imprint","IMPRINT",FACE,{"disambiguationData":[TD([[makeQuery(id+"F4.imprint","IMPRINT",EDGE,{"disambiguationData":[TD([[subQ2,-1.0]])],"derivedFrom":subQ1}),-1.0]])]});}
            var Q3;
            {var subQ0=sQuery(id+"F4.wireOp",EDGE,"E22");var subQ1=sQuery(id+"F4.wireOp",EDGE,"E15");var subQ2=makeQuery(id+"F4.imprint","INTERSECT",VERTEX,{"derivedFrom":[subQ1,subQ0]});Q3=makeQuery(id+"F4.imprint","IMPRINT",FACE,{"disambiguationData":[TD([[makeQuery(id+"F4.imprint","IMPRINT",EDGE,{"disambiguationData":[TD([[subQ2,-1.0]])],"derivedFrom":subQ1}),-1.0]])]});}
            extrude(context, id + "F10", {"entities" : qUnion([Q0, Q1, Q2, Q3]), "operationType" : NewBodyOperationType.REMOVE, "depth" : 44.45 * mm, "offsetDistance" : 25.4 * mm});
        }
        {
            var Q0;
            {var subQ0=sQuery(id+"F4.wireOp",EDGE,"E28.MirrorCS");var subQ1=sQuery(id+"F4.wireOp",EDGE,"E19.MirrorCS");var subQ2=makeQuery(id+"F4.imprint","INTERSECT",VERTEX,{"derivedFrom":[subQ1,subQ0]});Q0=makeQuery(id+"F4.imprint","IMPRINT",FACE,{"disambiguationData":[TD([[makeQuery(id+"F4.imprint","IMPRINT",EDGE,{"disambiguationData":[TD([[subQ2,-1.0]])],"derivedFrom":subQ1}),1.0]])]});}
            var Q1;
            {var subQ0=sQuery(id+"F4.wireOp",EDGE,"E22");var subQ1=sQuery(id+"F4.wireOp",EDGE,"E19.MirrorCS");var subQ2=makeQuery(id+"F4.imprint","INTERSECT",VERTEX,{"derivedFrom":[subQ1,subQ0]});Q1=makeQuery(id+"F4.imprint","IMPRINT",FACE,{"disambiguationData":[TD([[makeQuery(id+"F4.imprint","IMPRINT",EDGE,{"disambiguationData":[TD([[subQ2,-1.0]])],"derivedFrom":subQ1}),1.0]])]});}
            var Q2;
            {var subQ0=sQuery(id+"F4.wireOp",EDGE,"E22");var subQ1=sQuery(id+"F4.wireOp",EDGE,"E15");var subQ2=makeQuery(id+"F4.imprint","INTERSECT",VERTEX,{"derivedFrom":[subQ1,subQ0]});Q2=makeQuery(id+"F4.imprint","IMPRINT",FACE,{"disambiguationData":[TD([[makeQuery(id+"F4.imprint","IMPRINT",EDGE,{"disambiguationData":[TD([[subQ2,-1.0]])],"derivedFrom":subQ1}),-1.0]])]});}
            var Q3;
            {var subQ0=sQuery(id+"F4.wireOp",EDGE,"E23");var subQ1=sQuery(id+"F4.wireOp",EDGE,"E15");var subQ2=makeQuery(id+"F4.imprint","INTERSECT",VERTEX,{"derivedFrom":[subQ1,subQ0]});Q3=makeQuery(id+"F4.imprint","IMPRINT",FACE,{"disambiguationData":[TD([[makeQuery(id+"F4.imprint","IMPRINT",EDGE,{"disambiguationData":[TD([[subQ2,-1.0]])],"derivedFrom":subQ1}),-1.0]])]});}
            extrude(context, id + "F11", {"entities" : qUnion([Q0, Q1, Q2, Q3]), "operationType" : NewBodyOperationType.ADD, "depth" : 5.08 * mm, "offsetDistance" : 25.4 * mm});
        }
        {
            var Q0;
            {var subQ0=sQuery(id+"F4.wireOp",EDGE,"E23");var subQ1=sQuery(id+"F4.wireOp",EDGE,"E15");var subQ2=makeQuery(id+"F4.imprint","INTERSECT",VERTEX,{"derivedFrom":[subQ1,subQ0]});Q0=makeQuery(id+"F4.imprint","IMPRINT",FACE,{"disambiguationData":[TD([[makeQuery(id+"F4.imprint","IMPRINT",EDGE,{"disambiguationData":[TD([[subQ2,-1.0]])],"derivedFrom":subQ1}),-1.0]])]});}
            var Q1;
            {var subQ0=sQuery(id+"F4.wireOp",EDGE,"E22");var subQ1=sQuery(id+"F4.wireOp",EDGE,"E15");var subQ2=makeQuery(id+"F4.imprint","INTERSECT",VERTEX,{"derivedFrom":[subQ1,subQ0]});Q1=makeQuery(id+"F4.imprint","IMPRINT",FACE,{"disambiguationData":[TD([[makeQuery(id+"F4.imprint","IMPRINT",EDGE,{"disambiguationData":[TD([[subQ2,-1.0]])],"derivedFrom":subQ1}),-1.0]])]});}
            var Q2;
            {var subQ0=sQuery(id+"F4.wireOp",EDGE,"E15");var subQ1=sQuery(id+"F4.wireOp",EDGE,"E10");var subQ2=makeQuery(id+"F4.imprint","INTERSECT",VERTEX,{"derivedFrom":[subQ1,subQ0]});Q2=makeQuery(id+"F4.imprint","IMPRINT",FACE,{"disambiguationData":[TD([[makeQuery(id+"F4.imprint","IMPRINT",EDGE,{"disambiguationData":[TD([[subQ2,-1.0]])],"derivedFrom":subQ1}),-1.0]])]});}
            var Q3;
            {var subQ0=sQuery(id+"F4.wireOp",EDGE,"E10");var subQ1=makeQuery(id+"F4.imprint","INTERSECT",VERTEX,{"derivedFrom":[subQ0,sQuery(id+"F4.wireOp",EDGE,"E15")]});Q3=makeQuery(id+"F4.imprint","IMPRINT",FACE,{"disambiguationData":[TD([[makeQuery(id+"F4.imprint","IMPRINT",EDGE,{"disambiguationData":[TD([[subQ1,1.0]])],"derivedFrom":subQ0}),1.0]])]});}
            var Q4;
            {var subQ0=sQuery(id+"F4.wireOp",EDGE,"E19.MirrorCS");var subQ1=sQuery(id+"F4.wireOp",EDGE,"E10");var subQ2=makeQuery(id+"F4.imprint","INTERSECT",VERTEX,{"derivedFrom":[subQ1,subQ0]});Q4=makeQuery(id+"F4.imprint","IMPRINT",FACE,{"disambiguationData":[TD([[makeQuery(id+"F4.imprint","IMPRINT",EDGE,{"disambiguationData":[TD([[subQ2,1.0]])],"derivedFrom":subQ1}),-1.0]])]});}
            var Q5;
            {var subQ0=sQuery(id+"F4.wireOp",EDGE,"E22");var subQ1=sQuery(id+"F4.wireOp",EDGE,"E19.MirrorCS");var subQ2=makeQuery(id+"F4.imprint","INTERSECT",VERTEX,{"derivedFrom":[subQ1,subQ0]});Q5=makeQuery(id+"F4.imprint","IMPRINT",FACE,{"disambiguationData":[TD([[makeQuery(id+"F4.imprint","IMPRINT",EDGE,{"disambiguationData":[TD([[subQ2,-1.0]])],"derivedFrom":subQ1}),1.0]])]});}
            var Q6;
            {var subQ0=sQuery(id+"F4.wireOp",EDGE,"E28.MirrorCS");var subQ1=sQuery(id+"F4.wireOp",EDGE,"E19.MirrorCS");var subQ2=makeQuery(id+"F4.imprint","INTERSECT",VERTEX,{"derivedFrom":[subQ1,subQ0]});Q6=makeQuery(id+"F4.imprint","IMPRINT",FACE,{"disambiguationData":[TD([[makeQuery(id+"F4.imprint","IMPRINT",EDGE,{"disambiguationData":[TD([[subQ2,-1.0]])],"derivedFrom":subQ1}),1.0]])]});}
            extrude(context, id + "F12", {"entities" : qUnion([Q0, Q1, Q2, Q3, Q4, Q5, Q6]), "operationType" : NewBodyOperationType.REMOVE, "depth" : 2.54 * mm, "offsetDistance" : 25.4 * mm});
        }
        {
            var Q0;
            {var subQ0=sQuery(id+"F4.wireOp",EDGE,"E10");var subQ1=makeQuery(id+"F4.imprint","INTERSECT",VERTEX,{"derivedFrom":[subQ0,sQuery(id+"F4.wireOp",EDGE,"E15")]});Q0=makeQuery(id+"F4.imprint","IMPRINT",FACE,{"disambiguationData":[TD([[makeQuery(id+"F4.imprint","IMPRINT",EDGE,{"disambiguationData":[TD([[subQ1,1.0]])],"derivedFrom":subQ0}),1.0]])]});}
            extrude(context, id + "F13", {"entities" : qUnion([Q0]), "operationType" : NewBodyOperationType.REMOVE, "depth" : 49.53 * mm, "offsetDistance" : 25.4 * mm});
        }
        {
            var Q0;
            Q0=qCreatedBy(makeId("Top.planeOp"),FACE);
            var sketch = newSketch(context, id + "F14", { "sketchPlane" : qUnion([Q0])});
            skLineSegment(sketch, "E34.bottom", {"start": v(-20, -25.4) * mm, "end": v(20, -25.4) * mm});
            skLineSegment(sketch, "E34.top", {"start": v(-20, -65.4) * mm, "end": v(20, -65.4) * mm});
            skLineSegment(sketch, "E34.left", {"start": v(-20, -25.4) * mm, "end": v(-20, -65.4) * mm});
            skLineSegment(sketch, "E34.right", {"start": v(20, -25.4) * mm, "end": v(20, -65.4) * mm});
            skPoint(sketch, "E34.middle", {"position": v(0, -45.4) * mm});
            skLineSegment(sketch, "E35.bottom", {"start": v(-20, -27.62) * mm, "end": v(16.2, -27.62) * mm});
            skLineSegment(sketch, "E35.top", {"start": v(-20, -63.18) * mm, "end": v(16.2, -63.18) * mm});
            skLineSegment(sketch, "E35.left", {"start": v(-20, -27.62) * mm, "end": v(-20, -63.18) * mm});
            skLineSegment(sketch, "E35.right", {"start": v(16.2, -27.62) * mm, "end": v(16.2, -63.18) * mm});
            skPoint(sketch, "E36", {"position": v(-20, -45.4) * mm});
            skLineSegment(sketch, "E37.bottom", {"start": v(-20, -30.77) * mm, "end": v(-32.7, -30.77) * mm});
            skLineSegment(sketch, "E37.top", {"start": v(-20, -60.03) * mm, "end": v(-32.7, -60.03) * mm});
            skLineSegment(sketch, "E37.left", {"start": v(-20, -30.77) * mm, "end": v(-20, -60.03) * mm});
            skLineSegment(sketch, "E37.right", {"start": v(-32.7, -30.77) * mm, "end": v(-32.7, -60.03) * mm});
            skSolve(sketch);
        }
        {
            var Q0;
            {var subQ4=sQuery(id+"F14.wireOp",EDGE,"E34.bottom");Q0=makeQuery(id+"F14.imprint","IMPRINT",FACE,{"disambiguationData":[TD([[makeQuery(id+"F14.imprint","IMPRINT",EDGE,{"derivedFrom":subQ4}),-1.0]])]});}
            extrude(context, id + "F15", {"entities" : qUnion([Q0]), "depth" : 24.13 * mm, "offsetDistance" : 25.4 * mm});
        }
        {
            var Q0;
            {var subQ4=sQuery(id+"F14.wireOp",EDGE,"E35.bottom");Q0=makeQuery(id+"F14.imprint","IMPRINT",FACE,{"disambiguationData":[TD([[makeQuery(id+"F14.imprint","IMPRINT",EDGE,{"derivedFrom":subQ4}),-1.0]])]});}
            extrude(context, id + "F16", {"entities" : qUnion([Q0]), "operationType" : NewBodyOperationType.ADD, "depth" : 50.8 * mm, "offsetDistance" : 25.4 * mm});
        }
        {
            var Q0;
            Q0=makeQuery(id+"F14.imprint","IMPRINT",FACE,{"disambiguationData":[TD([[makeQuery(id+"F14.imprint","IMPRINT",EDGE,{"derivedFrom":sQuery(id+"F14.wireOp",EDGE,"E37.bottom")}),1.0]])]});
            extrude(context, id + "F17", {"entities" : qUnion([Q0]), "operationType" : NewBodyOperationType.ADD, "depth" : 50.8 * mm, "offsetDistance" : 25.4 * mm});
        }
        {
            var Q0;
            Q0=makeQuery(id+"F14.imprint","IMPRINT",FACE,{"disambiguationData":[TD([[makeQuery(id+"F14.imprint","IMPRINT",EDGE,{"derivedFrom":sQuery(id+"F14.wireOp",EDGE,"E37.bottom")}),1.0]])]});
            extrude(context, id + "F18", {"entities" : qUnion([Q0]), "operationType" : NewBodyOperationType.REMOVE, "depth" : 15.88 * mm, "offsetDistance" : 25.4 * mm});
        }
        {
            var Q0;
            Q0=makeQuery(id+"F14.imprint","IMPRINT",FACE,{"disambiguationData":[TD([[makeQuery(id+"F14.imprint","IMPRINT",EDGE,{"derivedFrom":sQuery(id+"F14.wireOp",EDGE,"E37.bottom")}),1.0]])]});
            extrude(context, id + "F19", {"entities" : qUnion([Q0]), "operationType" : NewBodyOperationType.REMOVE, "depth" : 25.4 * mm, "offsetDistance" : 25.4 * mm});
        }
        {
            var Q0;
            Q0=makeQuery(id+"F15.opExtrude","SWEPT_FACE",FACE,{"disambiguationData":[OSD([sQuery(id+"F14.wireOp",EDGE,"E34.bottom")])]});
            var sketch = newSketch(context, id + "F20", { "sketchPlane" : qUnion([Q0])});
            skCircle(sketch, "E38", {"center": v(0, -5.02) * mm, "radius": 13.9 * mm});
            skLineSegment(sketch, "E39", {"start": v(-19.69, 0) * mm, "end": v(-19.69, -10.03) * mm});
            skLineSegment(sketch, "E40", {"start": v(19.69, 0) * mm, "end": v(19.69, -10.03) * mm});
            skLineSegment(sketch, "E41", {"start": v(-19.69, 0) * mm, "end": v(0, 10.87) * mm});
            skLineSegment(sketch, "E42", {"start": v(0, 10.87) * mm, "end": v(19.69, 0) * mm});
            skLineSegment(sketch, "E43", {"start": v(-19.68, -10.03) * mm, "end": v(0, -20.9) * mm});
            skLineSegment(sketch, "E44", {"start": v(0, -20.9) * mm, "end": v(19.69, -10.03) * mm});
            skCircle(sketch, "E45", {"center": v(0, -5.02) * mm, "radius": 12.7 * mm});
            skSolve(sketch);
        }
        {
            var Q0;
            {var subQ0=sQuery(id+"F20.wireOp",EDGE,"E42");var subQ1=sQuery(id+"F20.wireOp",EDGE,"E38");var subQ2=makeQuery(id+"F20.imprint","INTERSECT",VERTEX,{"derivedFrom":[subQ1,subQ0]});Q0=makeQuery(id+"F20.imprint","IMPRINT",FACE,{"disambiguationData":[TD([[makeQuery(id+"F20.imprint","IMPRINT",EDGE,{"disambiguationData":[TD([[subQ2,1.0]])],"derivedFrom":subQ1}),-1.0]])]});}
            var Q1;
            {var subQ0=sQuery(id+"F20.wireOp",EDGE,"E41");var subQ1=sQuery(id+"F20.wireOp",EDGE,"E38");var subQ2=makeQuery(id+"F20.imprint","INTERSECT",VERTEX,{"derivedFrom":[subQ1,subQ0]});Q1=makeQuery(id+"F20.imprint","IMPRINT",FACE,{"disambiguationData":[TD([[makeQuery(id+"F20.imprint","IMPRINT",EDGE,{"disambiguationData":[TD([[subQ2,-1.0]])],"derivedFrom":subQ1}),-1.0]])]});}
            var Q2;
            {var subQ0=sQuery(id+"F20.wireOp",EDGE,"E38");var subQ7=makeQuery(id+"F20.imprint","INTERSECT",VERTEX,{"derivedFrom":[subQ0,sQuery(id+"F20.wireOp",EDGE,"E42")]});Q2=makeQuery(id+"F20.imprint","IMPRINT",FACE,{"disambiguationData":[TD([[makeQuery(id+"F20.imprint","IMPRINT",EDGE,{"disambiguationData":[TD([[subQ7,1.0]])],"derivedFrom":subQ0}),1.0]])]});}
            extrude(context, id + "F21", {"entities" : qUnion([Q0, Q1, Q2]), "operationType" : NewBodyOperationType.REMOVE, "oppositeDirection" : true, "depth" : 5.08 * mm, "offsetDistance" : 25.4 * mm});
        }
        {
            var Q0;
            {var subQ0=sQuery(id+"F20.wireOp",EDGE,"E45");var subQ1=makeQuery(id+"F15.opExtrude","CAP_EDGE",EDGE,{"disambiguationData":[OSD([sQuery(id+"F14.wireOp",EDGE,"E34.bottom")])],"isStart":true});var subQ2=makeQuery(id+"F20.imprint","INTERSECT",VERTEX,{"disambiguationData":[OD(0.0)],"derivedFrom":[subQ1,subQ0]});Q0=makeQuery(id+"F20.imprint","IMPRINT",FACE,{"disambiguationData":[TD([[makeQuery(id+"F20.imprint","IMPRINT",EDGE,{"disambiguationData":[TD([[subQ2,-1.0]])],"derivedFrom":subQ0}),1.0]])]});}
            var Q1;
            Q1=makeQuery(id+"F15.opExtrude","SWEPT_FACE",FACE,{"disambiguationData":[OSD([sQuery(id+"F14.wireOp",EDGE,"E34.top")])]});
            extrude(context, id + "F22", {"entities" : qUnion([Q0]), "operationType" : NewBodyOperationType.REMOVE, "endBound" : BoundingType.UP_TO_SURFACE, "oppositeDirection" : true, "depth" : 25.4 * mm, "endBoundEntityFace" : qUnion([Q1]), "offsetDistance" : 25.4 * mm});
        }
    });
